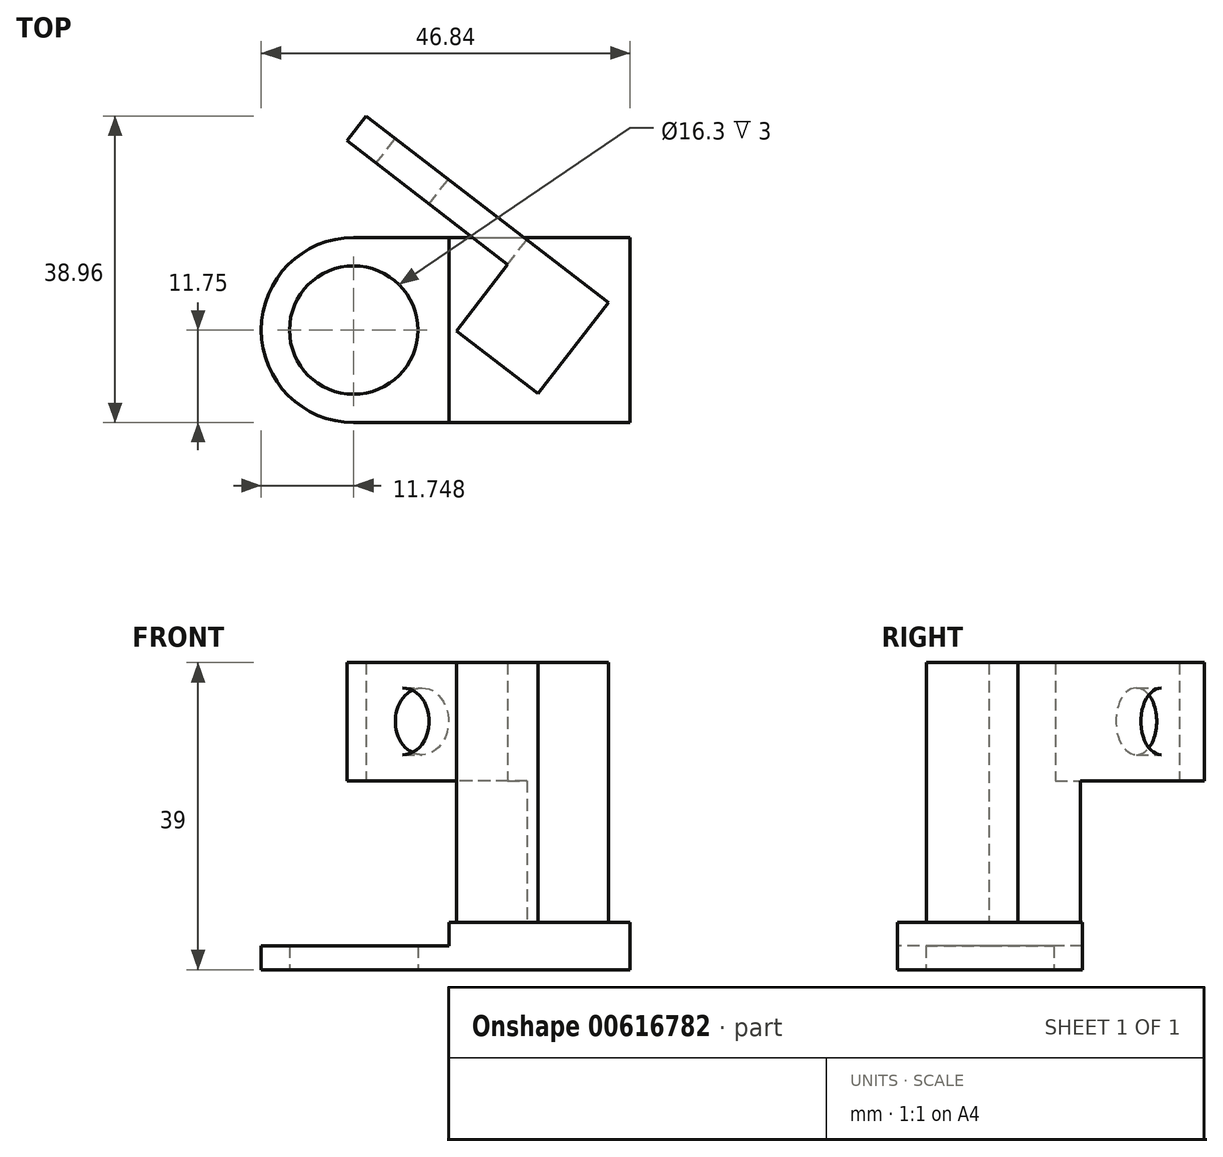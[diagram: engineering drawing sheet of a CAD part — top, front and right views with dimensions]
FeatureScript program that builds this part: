
annotation { "Feature Type Name" : "Feature", "Feature Type Description" : "" }
export const myFeature = defineFeature(function(context is Context, id is Id, definition is map)
    precondition{}
    {
        {
            var Q0;
            Q0=qCreatedBy(makeId("Top.planeOp"),FACE);
            var sketch = newSketch(context, id + "F0", { "sketchPlane" : qUnion([Q0])});
            skCircle(sketch, "E0", {"center": v(-3.34, 0) * mm, "radius": 8.15 * mm});
            skArc(sketch, "E1", {"start": v(-3.34, 11.75) * mm, "mid": v(-15.1, 0) * mm, "end": v(-3.34, -11.75) * mm});
            skLineSegment(sketch, "E2.bottom", {"start": v(-3.34, 11.75) * mm, "end": v(8.75, 11.75) * mm});
            skLineSegment(sketch, "E2.top", {"start": v(-3.34, -11.75) * mm, "end": v(8.75, -11.75) * mm});
            skLineSegment(sketch, "E3", {"start": v(8.75, 11.75) * mm, "end": v(8.75, -11.75) * mm});
            skSolve(sketch);
        }
        {
            var Q0;
            Q0=makeQuery(id+"F0.imprint","IMPRINT",FACE,{"disambiguationData":[TD([[makeQuery(id+"F0.imprint","IMPRINT",EDGE,{"derivedFrom":sQuery(id+"F0.wireOp",EDGE,"E0")}),-1.0]])]});
            extrude(context, id + "F1", {"entities" : qUnion([Q0]), "depth" : 3 * mm, "offsetDistance" : 25 * mm});
        }
        {
            var Q0;
            Q0=qCreatedBy(makeId("Top.planeOp"),FACE);
            var sketch = newSketch(context, id + "F2", { "sketchPlane" : qUnion([Q0])});
            skLineSegment(sketch, "E4.bottom", {"start": v(8.75, -11.75) * mm, "end": v(31.75, -11.75) * mm});
            skLineSegment(sketch, "E4.top", {"start": v(8.75, 11.75) * mm, "end": v(31.75, 11.75) * mm});
            skLineSegment(sketch, "E4.left", {"start": v(8.75, -11.75) * mm, "end": v(8.75, 11.75) * mm});
            skLineSegment(sketch, "E4.right", {"start": v(31.75, -11.75) * mm, "end": v(31.75, 11.75) * mm});
            skSolve(sketch);
        }
        {
            var Q0;
            Q0=makeQuery(id+"F2.imprint","IMPRINT",FACE,{"disambiguationData":[TD([[makeQuery(id+"F2.imprint","IMPRINT",EDGE,{"derivedFrom":sQuery(id+"F2.wireOp",EDGE,"E4.bottom")}),1.0]])]});
            extrude(context, id + "F3", {"entities" : qUnion([Q0]), "operationType" : NewBodyOperationType.ADD, "depth" : 6 * mm, "offsetDistance" : 25 * mm});
        }
        {
            var Q0;
            Q0=makeQuery(id+"F3.opExtrude","CAP_FACE",FACE,{"disambiguationData":[OSD([sQuery(id+"F2.wireOp",EDGE,"E4.bottom"),sQuery(id+"F2.wireOp",EDGE,"E4.top"),sQuery(id+"F2.wireOp",EDGE,"E4.left"),sQuery(id+"F2.wireOp",EDGE,"E4.right")])],"isStart":false});
            var sketch = newSketch(context, id + "F4", { "sketchPlane" : qUnion([Q0])});
            skLineSegment(sketch, "E5.bottom", {"start": v(14.35, -7.21) * mm, "end": v(27.41, -7.21) * mm});
            skLineSegment(sketch, "E5.top", {"start": v(14.35, 7.43) * mm, "end": v(27.41, 7.43) * mm});
            skLineSegment(sketch, "E5.left", {"start": v(14.35, -7.21) * mm, "end": v(14.35, 7.43) * mm});
            skLineSegment(sketch, "E5.right", {"start": v(27.41, -7.21) * mm, "end": v(27.41, 7.43) * mm});
            skSolve(sketch);
        }
        {
            var Q0;
            Q0=makeQuery(id+"F4.imprint","IMPRINT",FACE,{"disambiguationData":[TD([[makeQuery(id+"F4.imprint","IMPRINT",EDGE,{"derivedFrom":sQuery(id+"F4.wireOp",EDGE,"E5.bottom")}),1.0]])]});
            extrude(context, id + "F5", {"entities" : qUnion([Q0]), "depth" : 33 * mm, "offsetDistance" : 25 * mm});
        }
        {
            var Q0;
            Q0=makeQuery(id+"F5.opExtrude","SWEPT_FACE",FACE,{"disambiguationData":[OSD([sQuery(id+"F4.wireOp",EDGE,"E5.top")])]});
            var sketch = newSketch(context, id + "F6", { "sketchPlane" : qUnion([Q0])});
            skLineSegment(sketch, "E6.bottom", {"start": v(-27.41, 39) * mm, "end": v(11.4, 39) * mm});
            skLineSegment(sketch, "E6.top", {"start": v(-27.41, 23.98) * mm, "end": v(11.4, 23.98) * mm});
            skLineSegment(sketch, "E6.left", {"start": v(-27.41, 39) * mm, "end": v(-27.41, 23.98) * mm});
            skLineSegment(sketch, "E6.right", {"start": v(11.4, 39) * mm, "end": v(11.4, 23.98) * mm});
            skCircle(sketch, "E7", {"center": v(2.49, 31.54) * mm, "radius": 4.25 * mm});
            skSolve(sketch);
        }
        {
            var Q0;
            {var subQ0=sQuery(id+"F6.wireOp",EDGE,"E6.right");Q0=makeQuery(id+"F6.imprint","IMPRINT",FACE,{"disambiguationData":[TD([[makeQuery(id+"F6.imprint","IMPRINT",EDGE,{"derivedFrom":subQ0}),-1.0]])]});}
            extrude(context, id + "F7", {"entities" : qUnion([Q0]), "operationType" : NewBodyOperationType.ADD, "oppositeDirection" : true, "depth" : 4 * mm, "offsetDistance" : 25 * mm});
        }
        {
            var Q0;
            Q0=makeQuery(id+"F5.opExtrude","SWEPT_BODY",BODY,{"disambiguationData":[OSD([sQuery(id+"F4.wireOp",EDGE,"E5.bottom"),sQuery(id+"F4.wireOp",EDGE,"E5.top"),sQuery(id+"F4.wireOp",EDGE,"E5.left"),sQuery(id+"F4.wireOp",EDGE,"E5.right")])]});
            var Q1;
            Q1=makeQuery(id+"F5.opExtrude","SWEPT_EDGE",EDGE,{"disambiguationData":[OSD([sQuery(id+"F4.wireOp",EDGE,"E5.top"),sQuery(id+"F4.wireOp",EDGE,"E5.right")])]});
            transform(context, id + "F8", {"entities" : qUnion([Q0]), "transformType" : TransformType.TRANSLATION_3D, "dx" : 0 * mm, "dy" : -1.6 * mm, "dz" : 0 * mm, "makeCopy" : false});
        }
        {
            var Q0;
            Q0=makeQuery(id+"F5.opExtrude","SWEPT_BODY",BODY,{"disambiguationData":[OSD([sQuery(id+"F4.wireOp",EDGE,"E5.bottom"),sQuery(id+"F4.wireOp",EDGE,"E5.top"),sQuery(id+"F4.wireOp",EDGE,"E5.left"),sQuery(id+"F4.wireOp",EDGE,"E5.right")])]});
            var Q1;
            Q1=makeQuery(id+"F5.opExtrude","SWEPT_EDGE",EDGE,{"disambiguationData":[OSD([sQuery(id+"F4.wireOp",EDGE,"E5.top"),sQuery(id+"F4.wireOp",EDGE,"E5.right")])]});
            transform(context, id + "F9", {"entities" : qUnion([Q0]), "transformType" : TransformType.ROTATION, "transformAxis" : qUnion([Q1]), "angle" : 37.6 * degree, "makeCopy" : false});
        }
        {
            var Q0;
            Q0=makeQuery(id+"F5.opExtrude","SWEPT_BODY",BODY,{"disambiguationData":[OSD([sQuery(id+"F4.wireOp",EDGE,"E5.bottom"),sQuery(id+"F4.wireOp",EDGE,"E5.top"),sQuery(id+"F4.wireOp",EDGE,"E5.left"),sQuery(id+"F4.wireOp",EDGE,"E5.right")])]});
            transform(context, id + "F10", {"entities" : qUnion([Q0]), "transformType" : TransformType.TRANSLATION_3D, "dx" : 1.6 * mm, "dy" : -2.3 * mm, "dz" : 0 * mm, "makeCopy" : false});
        }
    });
